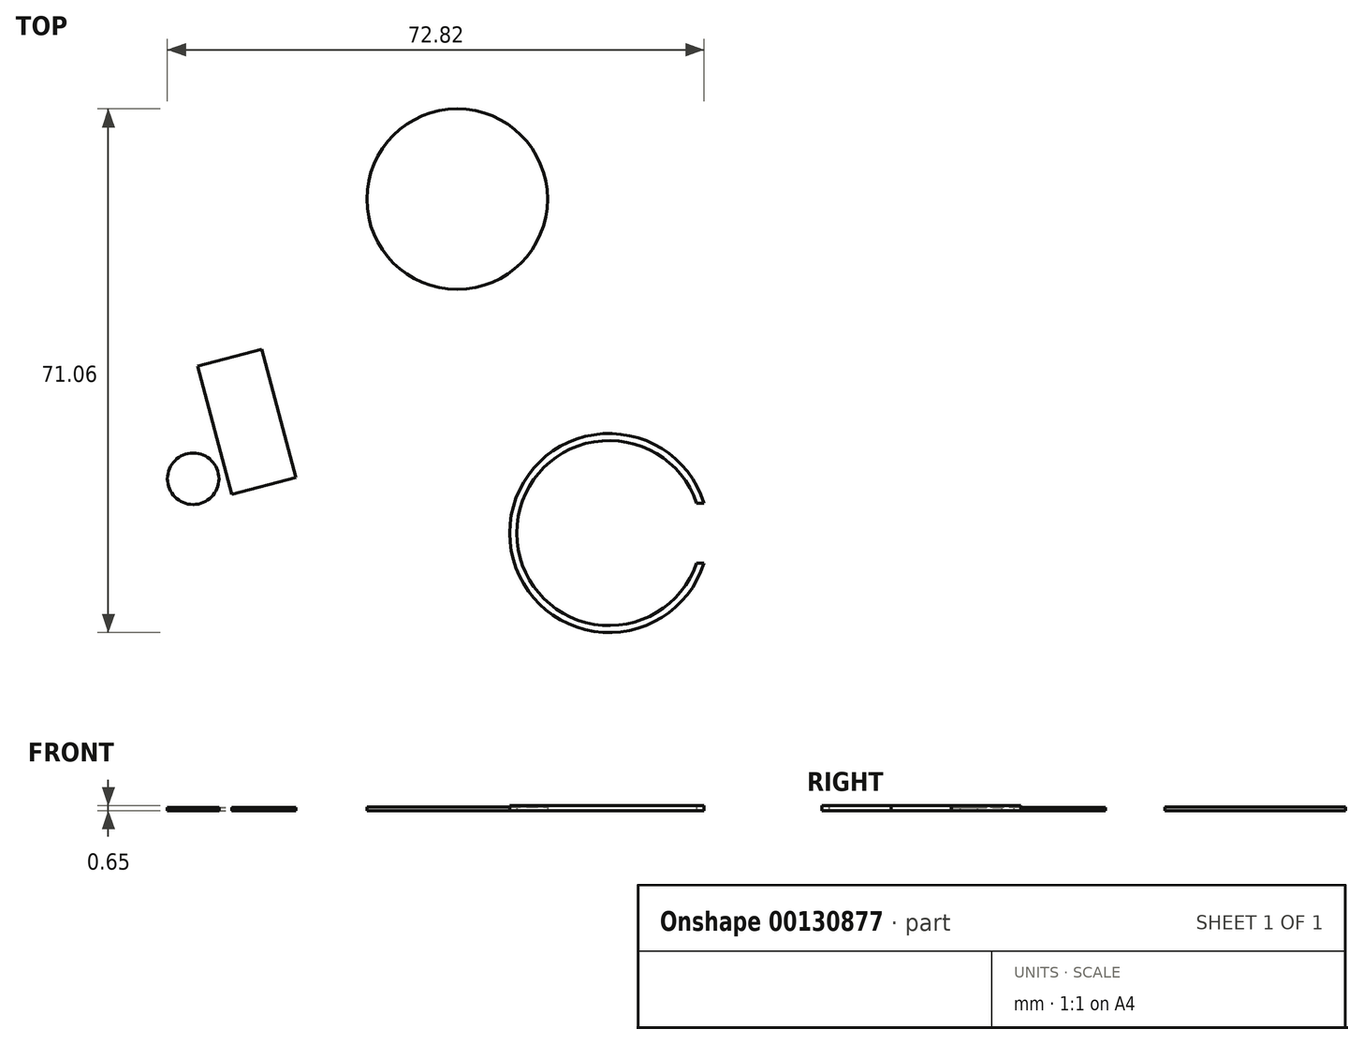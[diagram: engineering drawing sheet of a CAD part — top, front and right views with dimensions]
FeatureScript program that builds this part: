
annotation { "Feature Type Name" : "Feature", "Feature Type Description" : "" }
export const myFeature = defineFeature(function(context is Context, id is Id, definition is map)
    precondition{}
    {
        {
            var Q0;
            Q0=qCreatedBy(makeId("Top.planeOp"),FACE);
            var sketch = newSketch(context, id + "F0", { "sketchPlane" : qUnion([Q0])});
            skCircle(sketch, "E0", {"center": v(-23.37, 19.1) * mm, "radius": 3.5 * mm});
            skLineSegment(sketch, "E1.bottom", {"start": v(-22.77, 34.36) * mm, "end": v(-14.08, 36.7) * mm});
            skLineSegment(sketch, "E1.top", {"start": v(-18.11, 16.97) * mm, "end": v(-9.42, 19.3) * mm});
            skLineSegment(sketch, "E1.left", {"start": v(-22.77, 34.36) * mm, "end": v(-18.11, 16.97) * mm});
            skLineSegment(sketch, "E1.right", {"start": v(-14.08, 36.7) * mm, "end": v(-9.42, 19.3) * mm});
            skCircle(sketch, "E2", {"center": v(33.08, 11.74) * mm, "radius": 12.55 * mm});
            skCircle(sketch, "E3", {"center": v(33.08, 11.74) * mm, "radius": 13.5 * mm});
            skLineSegment(sketch, "E4.bottom", {"start": v(44.08, 15.81) * mm, "end": v(47.08, 15.81) * mm});
            skLineSegment(sketch, "E4.top", {"start": v(44.08, 7.66) * mm, "end": v(47.08, 7.66) * mm});
            skPoint(sketch, "E5.visualSharp", {"position": v(47.08, 15.81) * mm});
            skPoint(sketch, "E6.visualSharp", {"position": v(47.08, 7.66) * mm});
            skPoint(sketch, "E7.visualSharp", {"position": v(44.08, 7.66) * mm});
            skPoint(sketch, "E8.visualSharp", {"position": v(44.08, 15.81) * mm});
            skLineSegment(sketch, "E9", {"start": v(47.08, 15.81) * mm, "end": v(47.08, 7.66) * mm});
            skLineSegment(sketch, "E10", {"start": v(44.08, 7.66) * mm, "end": v(44.08, 15.81) * mm});
            skCircle(sketch, "E11", {"center": v(12.46, 57.05) * mm, "radius": 12.25 * mm});
            skLineSegment(sketch, "E12", {"start": v(0, 0) * mm, "end": v(16.6, 0) * mm, "construction": true});
            skLineSegment(sketch, "E13", {"start": v(0, 0) * mm, "end": v(-3.56, 13.28) * mm, "construction": true});
            skSolve(sketch);
        }
        {
            var Q0;
            Q0=makeQuery(id+"F0.imprint","IMPRINT",FACE,{"disambiguationData":[TD([[makeQuery(id+"F0.imprint","IMPRINT",EDGE,{"derivedFrom":sQuery(id+"F0.wireOp",EDGE,"E0")}),1.0]])]});
            extrude(context, id + "F1", {"entities" : qUnion([Q0]), "depth" : .4 * mm});
        }
        {
            var Q0;
            Q0=makeQuery(id+"F0.imprint","IMPRINT",FACE,{"disambiguationData":[TD([[makeQuery(id+"F0.imprint","IMPRINT",EDGE,{"derivedFrom":sQuery(id+"F0.wireOp",EDGE,"E1.bottom")}),-1.0]])]});
            extrude(context, id + "F2", {"entities" : qUnion([Q0]), "depth" : .4 * mm});
        }
        {
            var Q0;
            {var subQ1=sQuery(id+"F0.wireOp",EDGE,"E2");var subQ5=sQuery(id+"F0.wireOp",EDGE,"E4.bottom");var subQ6=makeQuery(id+"F0.imprint","INTERSECT",VERTEX,{"derivedFrom":[subQ1,subQ5]});Q0=makeQuery(id+"F0.imprint","IMPRINT",FACE,{"disambiguationData":[TD([[makeQuery(id+"F0.imprint","IMPRINT",EDGE,{"disambiguationData":[TD([[subQ6,-1.0]])],"derivedFrom":subQ1}),-1.0]])]});}
            extrude(context, id + "F3", {"entities" : qUnion([Q0]), "depth" : .65 * mm});
        }
        {
            var Q0;
            Q0=makeQuery(id+"F0.imprint","IMPRINT",FACE,{"disambiguationData":[TD([[makeQuery(id+"F0.imprint","IMPRINT",EDGE,{"derivedFrom":sQuery(id+"F0.wireOp",EDGE,"E11")}),1.0]])]});
            extrude(context, id + "F4", {"entities" : qUnion([Q0]), "depth" : .5 * mm});
        }
    });
